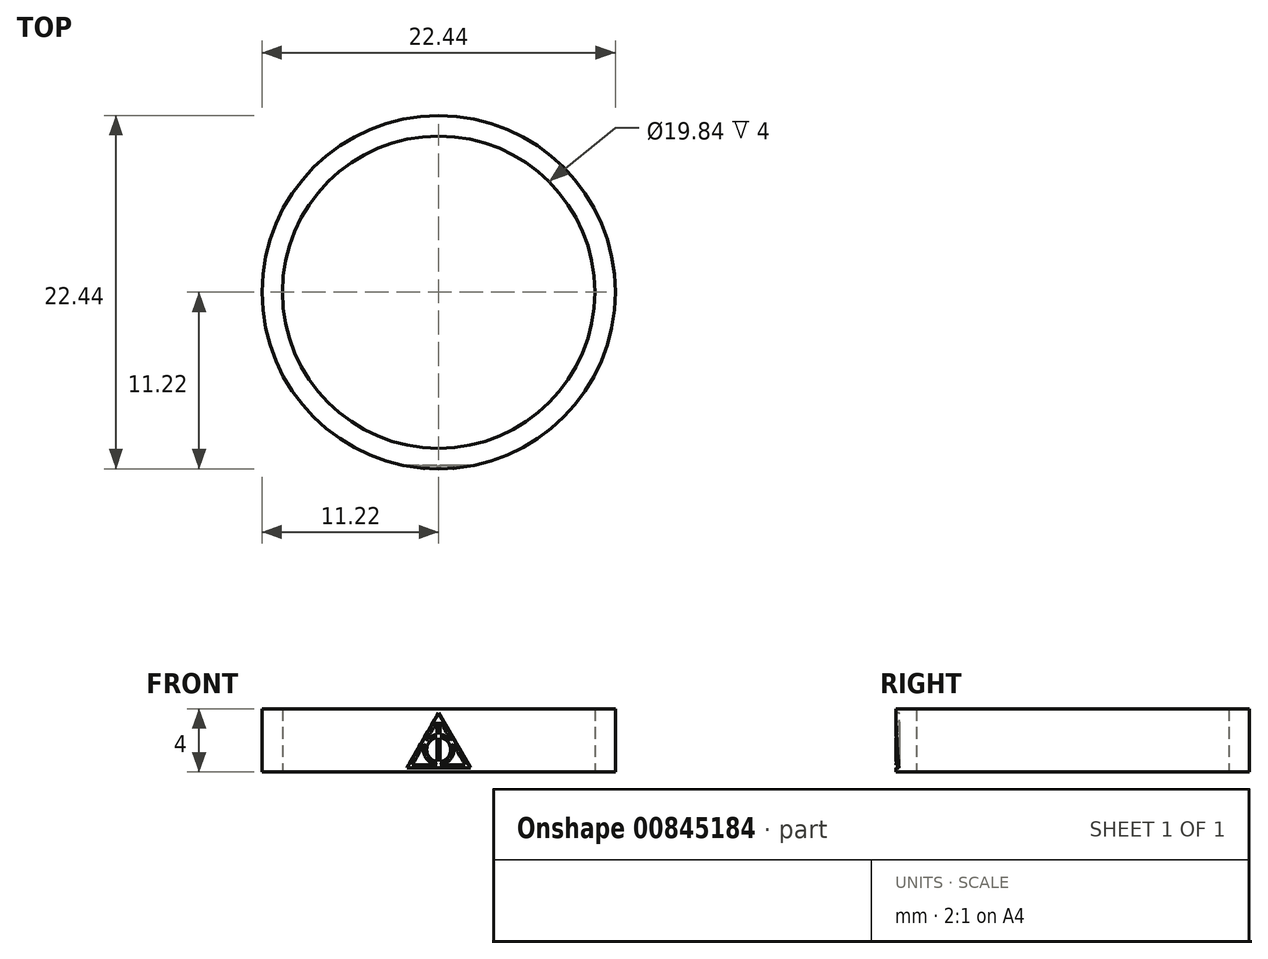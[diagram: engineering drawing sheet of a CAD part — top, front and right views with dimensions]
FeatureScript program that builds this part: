
annotation { "Feature Type Name" : "Feature", "Feature Type Description" : "" }
export const myFeature = defineFeature(function(context is Context, id is Id, definition is map)
    precondition{}
    {
        {
            var Q0;
            Q0=qCreatedBy(makeId("Top.planeOp"),FACE);
            var sketch = newSketch(context, id + "F0", { "sketchPlane" : qUnion([Q0])});
            skCircle(sketch, "E0", {"center": v(0, 0) * mm, "radius": 11.22 * mm});
            skCircle(sketch, "E1", {"center": v(0, 0) * mm, "radius": 9.92 * mm});
            skSolve(sketch);
        }
        {
            var Q0;
            Q0=makeQuery(id+"F0.imprint","IMPRINT",FACE,{"disambiguationData":[TD([[makeQuery(id+"F0.imprint","IMPRINT",EDGE,{"derivedFrom":sQuery(id+"F0.wireOp",EDGE,"E0")}),1.0]])]});
            extrude(context, id + "F1", {"entities" : qUnion([Q0]), "depth" : 4 * mm, "offsetDistance" : 25 * mm});
        }
        {
            var Q0;
            Q0=qCreatedBy(makeId("Front.planeOp"),FACE);
            cPlane(context, id + "F2", {"entities" : qUnion([Q0]), "cplaneType" : CPlaneType.OFFSET, "offset" : 11.3 * mm, "width" : 150 * mm, "height" : 150 * mm});
        }
        {
            var Q0;
            Q0=qCreatedBy(id+"F2.planeOp",FACE);
            var sketch = newSketch(context, id + "F3", { "sketchPlane" : qUnion([Q0])});
            skLineSegment(sketch, "E2", {"start": v(-2.02, 0.25) * mm, "end": v(0, 3.75) * mm});
            skLineSegment(sketch, "E3", {"start": v(0, 3.75) * mm, "end": v(2.02, 0.25) * mm});
            skLineSegment(sketch, "E4", {"start": v(2.02, 0.25) * mm, "end": v(-2.02, 0.25) * mm});
            skLineSegment(sketch, "E5", {"start": v(0, 0.25) * mm, "end": v(0, 1.42) * mm, "construction": true});
            skLineSegment(sketch, "E6", {"start": v(-1.67, 0.45) * mm, "end": v(-0.9, 1.78) * mm});
            skLineSegment(sketch, "E7", {"start": v(0.1, 3.18) * mm, "end": v(0.77, 2.02) * mm});
            skLineSegment(sketch, "E8", {"start": v(1.67, 0.45) * mm, "end": v(0.1, 0.45) * mm});
            skArc(sketch, "E9", {"start": v(0.1, 0.66) * mm, "mid": v(0.77, 1.42) * mm, "end": v(0.1, 2.18) * mm});
            skLineSegment(sketch, "E10", {"start": v(-0.1, 3.18) * mm, "end": v(-0.1, 2.38) * mm});
            skLineSegment(sketch, "E11.MirrorCS", {"start": v(0.1, 3.18) * mm, "end": v(0.1, 2.38) * mm});
            skLineSegment(sketch, "E12", {"start": v(-0.9, 1.78) * mm, "end": v(-0.9, 1.77) * mm});
            skLineSegment(sketch, "E13", {"start": v(-0.77, 2.02) * mm, "end": v(-0.76, 2.02) * mm});
            skArc(sketch, "E14", {"start": v(-0.9, 1.77) * mm, "mid": v(-0.83, 0.92) * mm, "end": v(-0.1, 0.46) * mm});
            skLineSegment(sketch, "E15", {"start": v(-0.77, 2.02) * mm, "end": v(-0.1, 3.18) * mm});
            skLineSegment(sketch, "E16.MirrorCS", {"start": v(0.77, 2.02) * mm, "end": v(0.77, 2.02) * mm});
            skLineSegment(sketch, "E17.MirrorCS", {"start": v(0.9, 1.78) * mm, "end": v(0.9, 1.78) * mm});
            skLineSegment(sketch, "E18", {"start": v(0.9, 1.78) * mm, "end": v(0.9, 1.77) * mm});
            skArc(sketch, "E19", {"start": v(0.76, 2.02) * mm, "mid": v(0.47, 2.26) * mm, "end": v(0.1, 2.38) * mm});
            skLineSegment(sketch, "E20", {"start": v(0.77, 2.02) * mm, "end": v(0.76, 2.02) * mm});
            skLineSegment(sketch, "E21.trimOffspring", {"start": v(0.9, 1.78) * mm, "end": v(1.67, 0.45) * mm});
            skArc(sketch, "E22.trimOffspring", {"start": v(0.1, 0.46) * mm, "mid": v(0.83, 0.92) * mm, "end": v(0.9, 1.77) * mm});
            skLineSegment(sketch, "E23.trimOffspring", {"start": v(-0.1, 0.45) * mm, "end": v(-1.67, 0.45) * mm});
            skLineSegment(sketch, "E24.trimOffspring", {"start": v(-0.1, 0.46) * mm, "end": v(-0.1, 0.45) * mm});
            skLineSegment(sketch, "E25.trimOffspring", {"start": v(0.1, 0.46) * mm, "end": v(0.1, 0.45) * mm});
            skArc(sketch, "E26.trimOffspring", {"start": v(-0.1, 2.18) * mm, "mid": v(-0.77, 1.42) * mm, "end": v(-0.1, 0.66) * mm});
            skArc(sketch, "E27.trimOffspring", {"start": v(-0.1, 2.38) * mm, "mid": v(-0.47, 2.26) * mm, "end": v(-0.76, 2.02) * mm});
            skLineSegment(sketch, "E28.trimOffspring", {"start": v(0.1, 2.18) * mm, "end": v(0.1, 0.66) * mm});
            skLineSegment(sketch, "E29.trimOffspring", {"start": v(-0.1, 2.18) * mm, "end": v(-0.1, 0.66) * mm});
            skLineSegment(sketch, "E30.trimOffspring", {"start": v(0, 3.35) * mm, "end": v(0, 3.75) * mm, "construction": true});
            skSolve(sketch);
        }
        {
            var Q0;
            Q0 = qSketchRegion(id + "F3", true);
            extrude(context, id + "F4", {"entities" : qUnion([Q0]), "operationType" : NewBodyOperationType.REMOVE, "oppositeDirection" : true, "depth" : 0.3 * mm, "offsetDistance" : 25 * mm});
        }
    });
